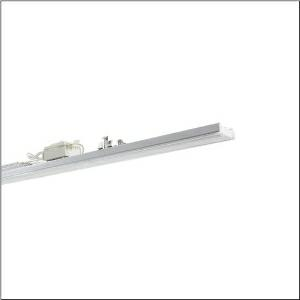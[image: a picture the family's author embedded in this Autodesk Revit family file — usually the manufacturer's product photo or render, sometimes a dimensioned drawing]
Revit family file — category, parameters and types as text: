
# Revit family: licross_21_recessed_mo_52tl19dv4e5g
name_source: partatom
category: Lighting Fixtures
units: mm (PartAtom-declared; Revit-internal decimal feet)

## family parameters
Cut with Voids When Loaded = No
Host = Face
Light Source = No
Part Type = Normal
Room Calculation Point = No
Round Connector Dimension = Use Diameter
Shared = No

## types (1)
- --- (1 x LED, 14780 lm, 85.3 W, 4000K)
    Apparent Load = 85 VA
    CIE Flux Codes = 55 90 98 100 100
    Color Rendering = 80
    Color Temperature = 4000K
    Default Elevation = 1800 mm
    Description = Licross 21 Recessed MO, luminaire insert, of sheet steel, galvanised, coil coated, white, length: 2.250mm, width: 66mm, height: 67mm, LED rated luminous flux: 14.780lm, light colour: 840, SDCM (Standard Deviation of Colour Matching)MacAdam ≤ 3 SDCM (initial), control gear: DALI 2, with plug, 5-pole, with phase selection, mains connection: 220..240V, AC, 50/60Hz, rated input power: 85W, internal wiring halogen-free, primary light control with lens, of plastic, primary optical cover: cover, of PMMA, light emission: direct distribution, primary light characteristic: double asymmetric, protection rating (complete): IP40, insulation class (complete): insulation class I (protective earthing), certification: CE, ENEC, VDE, UKCA, protection symbol: D if used in an environment without relevant dust loads with corresponding accessories, impact resistance: IK06, permissible ambient temperature for indoor applications: -25..+35°C, corresponds to IFS (International Featured Standards) requirements for safety and quality in the food industry, reducing of maximum allowable ambient temperature of 5°C with ceiling mounting, LABS conformity tested according to VDMA 24364:2018-05, The light source and the operating device comply with the requirements of the Ecodesign Regulation (EU) 2019/2020 and are replaceable in accordance with this regulation, packaging unit: 1 piece
    Height = 58 mm
    Lamp = 1 x LED
    Lamp Light Flux = 14780 lm
    Lamp Power = 85.3 W
    Lamp count = 1
    Length = 2250 mm
    Luminous efficacy = 173 lm/W
    Manufacturer = Siteco
    ModVariant = No
    Model = 52TL19DV4E5G
    Mounting Place = Ceiling
    Mounting Type = Pendant
    Number of Poles = 1
    OnlyDefault = Yes
    Power Factor = 1
    Product Name = Licross 21 Recessed MO
    Product group = luminaire insert | ceiling pendant
    ProductGroupID = 901
    Protection Class = Protection class I
    Protection Degree = IP 40
    RLX_Detail_Level = 1
    RLX_Emergency_Light_Flux = 0 lm
    RLX_Emergency_Type = 0
    RLX_Emergency_Type_DB = No
    RlxData = <blob elided: 29877 chars, md5=983e0a43>
    Socket = socket
    Standby Power = 0 W
    System Light Flux = 14780 lm
    System Power = 85 W
    Type Comments = factory setting: luminous flux: 100 % | dim-lin: 254 | 390 mA
    Type Image = l_1296930.jpg
    URL = http://relux.com
    VarID = @adj_128217
    Voltage = 0 V
    Weight = 0.00 kg
    Width = 66 mm

## geometry (parser evidence)
native form markers: Blend x4, Sweep x9
no freeform markers — native parametric forms only
